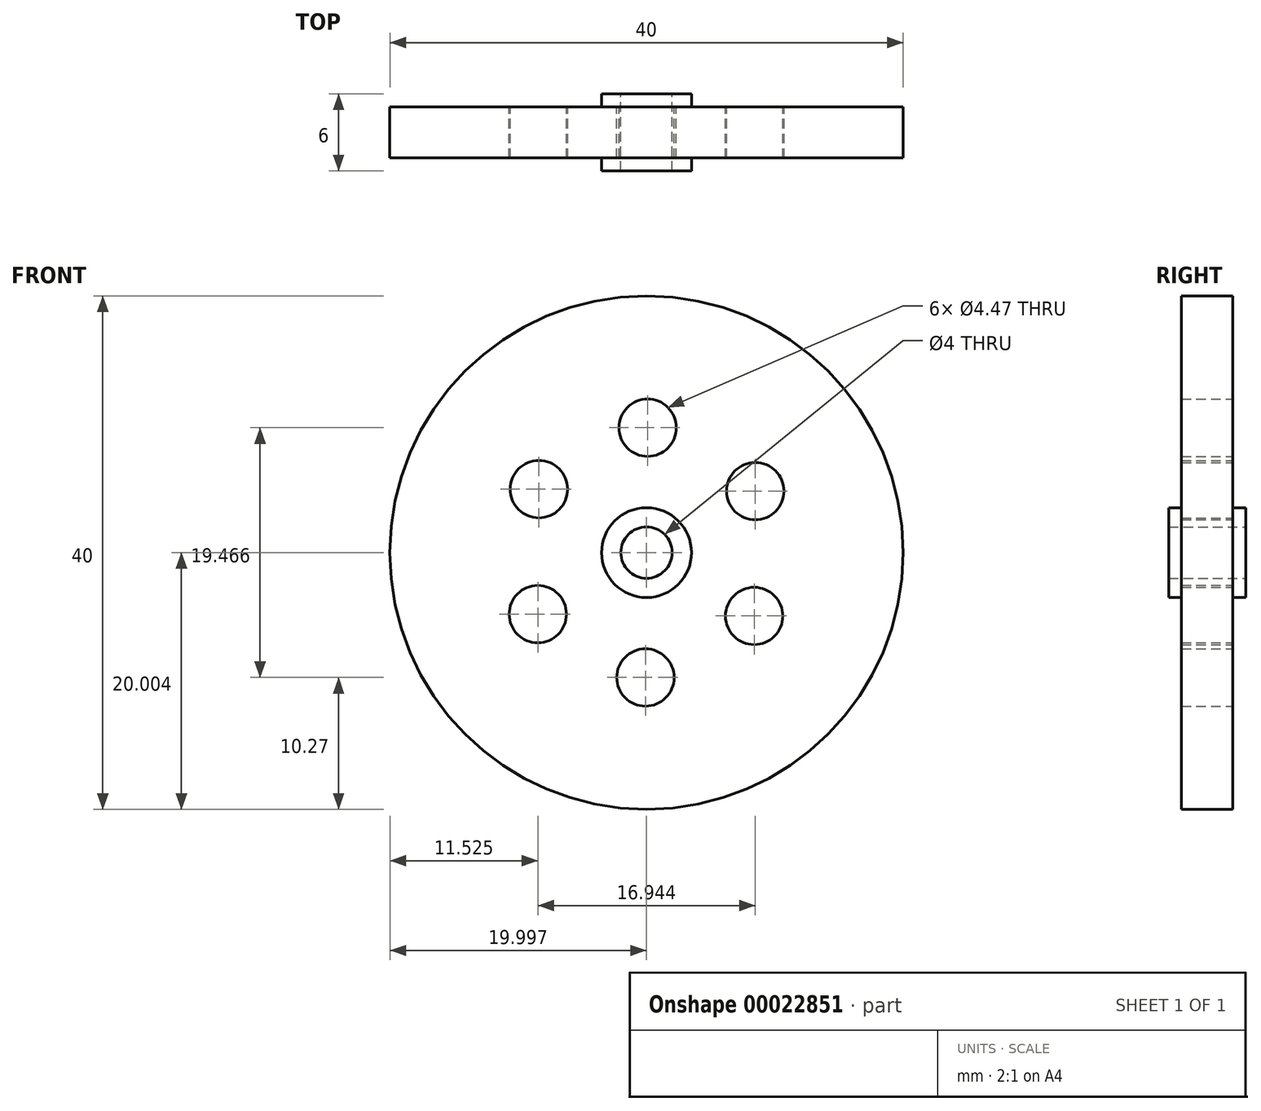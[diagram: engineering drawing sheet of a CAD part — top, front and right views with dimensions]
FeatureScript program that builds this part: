
annotation { "Feature Type Name" : "Feature", "Feature Type Description" : "" }
export const myFeature = defineFeature(function(context is Context, id is Id, definition is map)
    precondition{}
    {
        {
            var Q0;
            Q0=qCreatedBy(makeId("Front.planeOp"),FACE);
            var sketch = newSketch(context, id + "F0", { "sketchPlane" : qUnion([Q0])});
            skCircle(sketch, "E0", {"center": v(-3.81, -2.79) * mm, "radius": 20 * mm});
            skCircle(sketch, "E1", {"center": v(-3.81, -2.79) * mm, "radius": 3.5 * mm});
            skCircle(sketch, "E2", {"center": v(-3.81, -2.79) * mm, "radius": 2 * mm});
            skCircle(sketch, "E3", {"center": v(-3.73, 6.95) * mm, "radius": 2.23 * mm});
            skCircle(sketch, "E4.1.0", {"center": v(-12.2, 2.15) * mm, "radius": 2.23 * mm});
            skCircle(sketch, "E4.2.0", {"center": v(-12.29, -7.58) * mm, "radius": 2.23 * mm});
            skCircle(sketch, "E4.3.0", {"center": v(-3.9, -12.52) * mm, "radius": 2.23 * mm});
            skCircle(sketch, "E4.4.0", {"center": v(4.57, -7.73) * mm, "radius": 2.23 * mm});
            skCircle(sketch, "E4.5.0", {"center": v(4.66, 2) * mm, "radius": 2.23 * mm});
            skSolve(sketch);
        }
        {
            var Q0;
            Q0 = qSketchRegion(id + "F0", true);
            extrude(context, id + "F1", {"entities" : qUnion([Q0]), "endBound" : BoundingType.SYMMETRIC, "depth" : 4 * mm});
        }
        {
            var Q0;
            Q0=makeQuery(id+"F0.imprint","IMPRINT",FACE,{"disambiguationData":[TD([[makeQuery(id+"F0.imprint","IMPRINT",EDGE,{"derivedFrom":sQuery(id+"F0.wireOp",EDGE,"E1")}),1.0]])]});
            extrude(context, id + "F2", {"entities" : qUnion([Q0]), "operationType" : NewBodyOperationType.ADD, "endBound" : BoundingType.SYMMETRIC, "depth" : 6 * mm});
        }
    });
